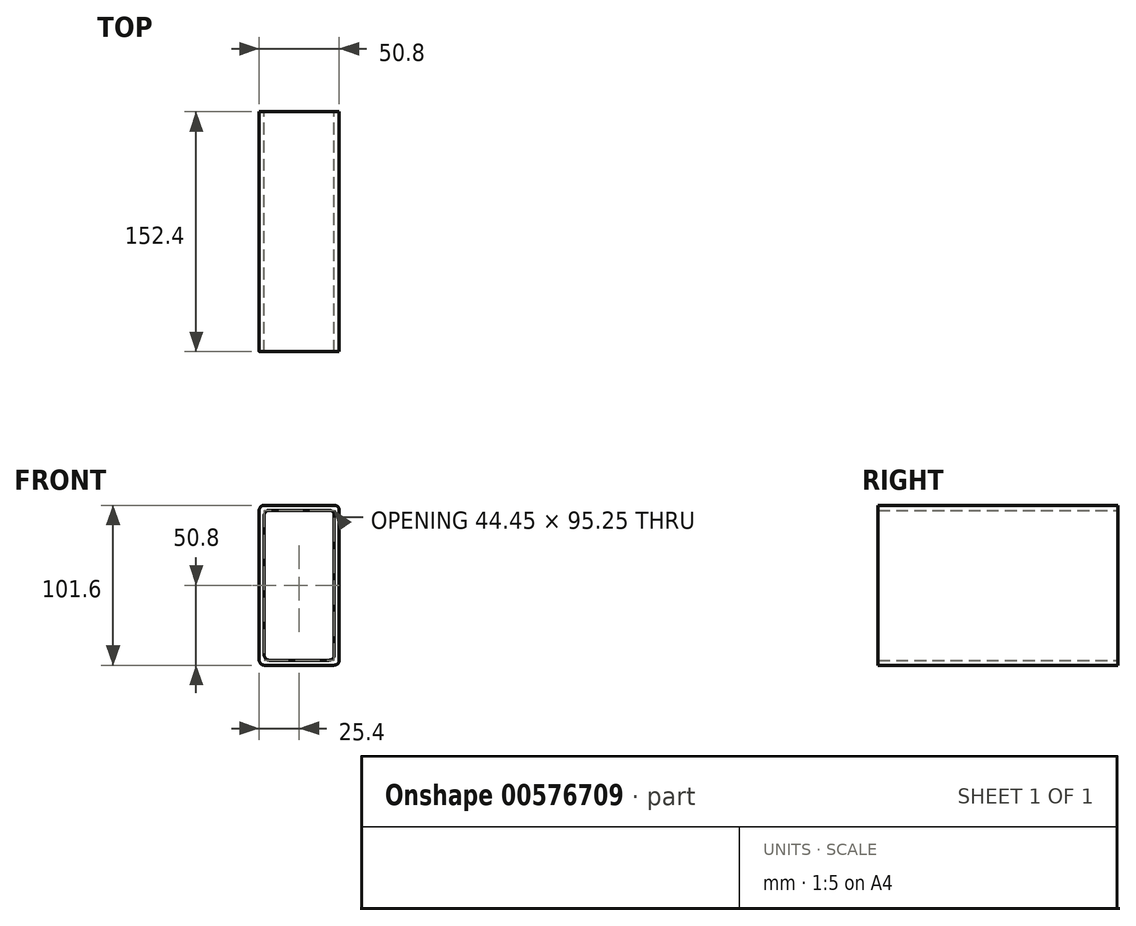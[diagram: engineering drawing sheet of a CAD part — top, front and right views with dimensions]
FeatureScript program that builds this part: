
annotation { "Feature Type Name" : "Feature", "Feature Type Description" : "" }
export const myFeature = defineFeature(function(context is Context, id is Id, definition is map)
    precondition{}
    {
        {
            var Q0;
            Q0=qCreatedBy(makeId("Front.planeOp"),FACE);
            var sketch = newSketch(context, id + "F0", { "sketchPlane" : qUnion([Q0])});
            skLineSegment(sketch, "E0.bottom", {"start": v(22.22, 50.8) * mm, "end": v(-22.23, 50.8) * mm});
            skLineSegment(sketch, "E0.top", {"start": v(22.23, -50.8) * mm, "end": v(-22.22, -50.8) * mm});
            skLineSegment(sketch, "E0.left", {"start": v(25.4, 47.62) * mm, "end": v(25.4, -47.62) * mm});
            skLineSegment(sketch, "E0.right", {"start": v(-25.4, 47.63) * mm, "end": v(-25.4, -47.62) * mm});
            skPoint(sketch, "E0.middle", {"position": v(0, 0) * mm});
            skLineSegment(sketch, "E1.0", {"start": v(19.05, 47.63) * mm, "end": v(-19.05, 47.63) * mm});
            skLineSegment(sketch, "E1.1", {"start": v(22.23, 44.45) * mm, "end": v(22.23, -44.45) * mm});
            skLineSegment(sketch, "E1.2", {"start": v(19.05, -47.63) * mm, "end": v(-19.05, -47.63) * mm});
            skLineSegment(sketch, "E1.3", {"start": v(-22.23, 44.45) * mm, "end": v(-22.22, -44.45) * mm});
            skPoint(sketch, "E2.visualSharp", {"position": v(-22.23, 47.63) * mm});
            skArc(sketch, "E2.filletArc", {"start": v(-19.05, 47.63) * mm, "mid": v(-21.3, 46.7) * mm, "end": v(-22.23, 44.45) * mm});
            skPoint(sketch, "E3.visualSharp", {"position": v(-25.4, 50.8) * mm});
            skArc(sketch, "E3.filletArc", {"start": v(-22.23, 50.8) * mm, "mid": v(-24.47, 49.87) * mm, "end": v(-25.4, 47.63) * mm});
            skPoint(sketch, "E4.visualSharp", {"position": v(22.23, 47.63) * mm});
            skArc(sketch, "E4.filletArc", {"start": v(22.23, 44.45) * mm, "mid": v(21.3, 46.7) * mm, "end": v(19.05, 47.63) * mm});
            skPoint(sketch, "E5.visualSharp", {"position": v(-22.22, -47.63) * mm});
            skArc(sketch, "E5.filletArc", {"start": v(-22.22, -44.45) * mm, "mid": v(-21.3, -46.7) * mm, "end": v(-19.05, -47.63) * mm});
            skPoint(sketch, "E6.visualSharp", {"position": v(22.23, -47.63) * mm});
            skArc(sketch, "E6.filletArc", {"start": v(19.05, -47.63) * mm, "mid": v(21.3, -46.7) * mm, "end": v(22.23, -44.45) * mm});
            skPoint(sketch, "E7.visualSharp", {"position": v(25.4, -50.8) * mm});
            skArc(sketch, "E7.filletArc", {"start": v(22.23, -50.8) * mm, "mid": v(24.47, -49.87) * mm, "end": v(25.4, -47.62) * mm});
            skPoint(sketch, "E8.visualSharp", {"position": v(-25.4, -50.8) * mm});
            skArc(sketch, "E8.filletArc", {"start": v(-25.4, -47.62) * mm, "mid": v(-24.47, -49.87) * mm, "end": v(-22.22, -50.8) * mm});
            skPoint(sketch, "E9.visualSharp", {"position": v(25.4, 50.8) * mm});
            skArc(sketch, "E9.filletArc", {"start": v(25.4, 47.62) * mm, "mid": v(24.47, 49.87) * mm, "end": v(22.22, 50.8) * mm});
            skSolve(sketch);
        }
        {
            var Q0;
            Q0 = qSketchRegion(id + "F0", true);
            extrude(context, id + "F1", {"entities" : qUnion([Q0]), "depth" : 152.4 * mm, "offsetDistance" : 25.4 * mm});
        }
    });
